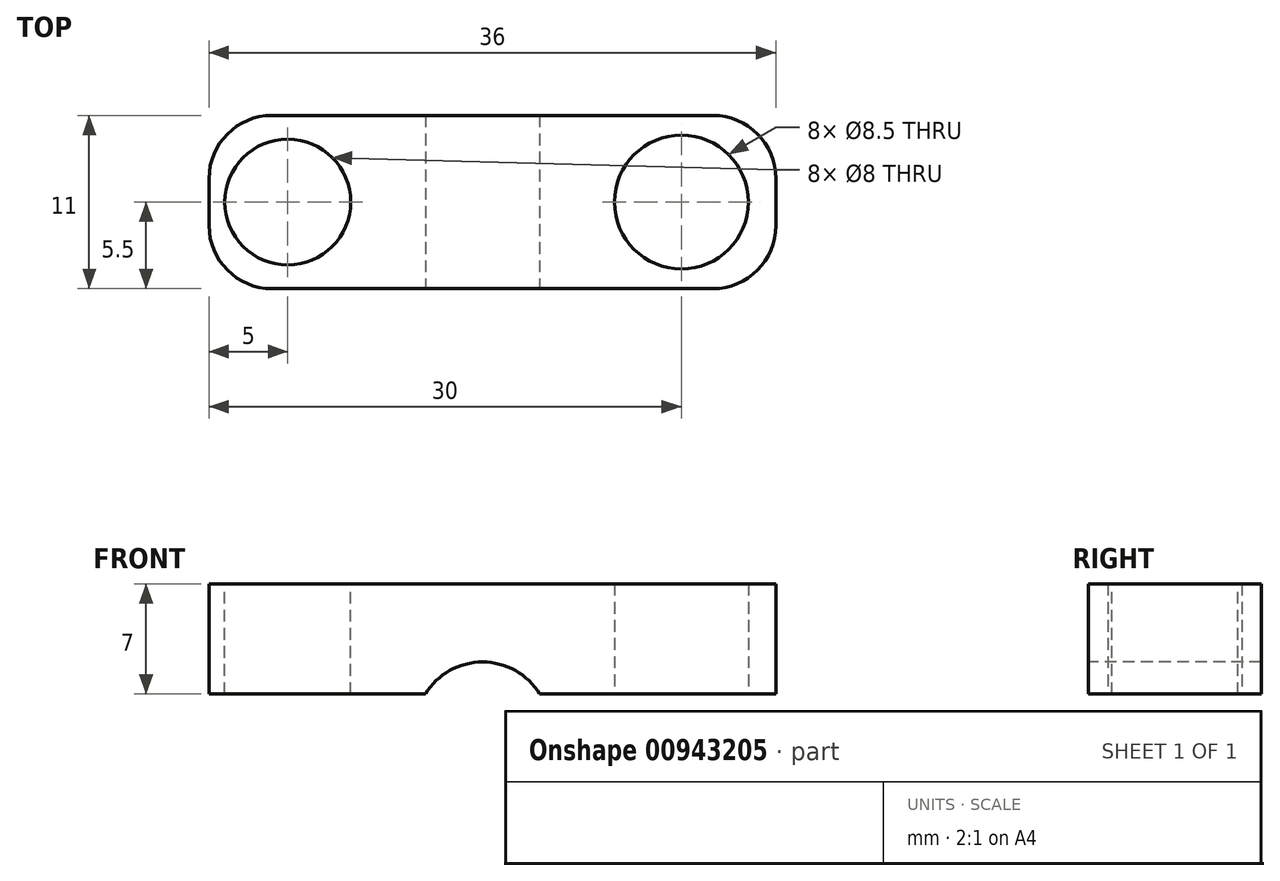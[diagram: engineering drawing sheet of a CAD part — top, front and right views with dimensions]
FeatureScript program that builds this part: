
annotation { "Feature Type Name" : "Feature", "Feature Type Description" : "" }
export const myFeature = defineFeature(function(context is Context, id is Id, definition is map)
    precondition{}
    {
        {
            var Q0;
            Q0=qCreatedBy(makeId("Top.planeOp"),FACE);
            var sketch = newSketch(context, id + "F0", { "sketchPlane" : qUnion([Q0])});
            skLineSegment(sketch, "E0.bottom", {"start": v(-26, 5.5) * mm, "end": v(2, 5.5) * mm});
            skLineSegment(sketch, "E0.top", {"start": v(-26, -5.5) * mm, "end": v(2, -5.5) * mm});
            skLineSegment(sketch, "E0.left", {"start": v(-30, 1.5) * mm, "end": v(-30, -1.5) * mm});
            skLineSegment(sketch, "E0.right", {"start": v(6, 1.5) * mm, "end": v(6, -1.5) * mm});
            skCircle(sketch, "E1", {"center": v(0, 0) * mm, "radius": 4.25 * mm});
            skPoint(sketch, "E2.visualSharp", {"position": v(-30, 5.5) * mm});
            skArc(sketch, "E2.filletArc", {"start": v(-26, 5.5) * mm, "mid": v(-28.83, 4.33) * mm, "end": v(-30, 1.5) * mm});
            skPoint(sketch, "E3.visualSharp", {"position": v(-30, -5.5) * mm});
            skArc(sketch, "E3.filletArc", {"start": v(-30, -1.5) * mm, "mid": v(-28.83, -4.33) * mm, "end": v(-26, -5.5) * mm});
            skPoint(sketch, "E4.visualSharp", {"position": v(6, -5.5) * mm});
            skArc(sketch, "E4.filletArc", {"start": v(2, -5.5) * mm, "mid": v(4.83, -4.33) * mm, "end": v(6, -1.5) * mm});
            skPoint(sketch, "E5.visualSharp", {"position": v(6, 5.5) * mm});
            skArc(sketch, "E5.filletArc", {"start": v(6, 1.5) * mm, "mid": v(4.83, 4.33) * mm, "end": v(2, 5.5) * mm});
            skSolve(sketch);
        }
        {
            var Q0;
            Q0=makeQuery(id+"F0.imprint","IMPRINT",FACE,{"disambiguationData":[TD([[makeQuery(id+"F0.imprint","IMPRINT",EDGE,{"derivedFrom":sQuery(id+"F0.wireOp",EDGE,"E0.bottom")}),-1.0]])]});
            extrude(context, id + "F1", {"entities" : qUnion([Q0]), "depth" : 7 * mm, "offsetDistance" : 25 * mm});
        }
        {
            var Q0;
            Q0=makeQuery(id+"F1.opExtrude","SWEPT_FACE",FACE,{"disambiguationData":[OSD([sQuery(id+"F0.wireOp",EDGE,"E0.top")])]});
            var sketch = newSketch(context, id + "F2", { "sketchPlane" : qUnion([Q0])});
            skArc(sketch, "E6", {"start": v(-9, 0) * mm, "mid": v(-12.63, 2.04) * mm, "end": v(-16.26, 0) * mm});
            skLineSegment(sketch, "E7", {"start": v(-16.26, 0) * mm, "end": v(-9, 0) * mm});
            skSolve(sketch);
        }
        {
            var Q0;
            Q0=qSketchRegion(id+"F2",true);
            extrude(context, id + "F3", {"entities" : qUnion([Q0]), "operationType" : NewBodyOperationType.REMOVE, "oppositeDirection" : true, "depth" : 25 * mm, "offsetDistance" : 25 * mm});
        }
        {
            var Q0;
            Q0=makeQuery(id+"F1.opExtrude","CAP_FACE",FACE,{"disambiguationData":[OSD([sQuery(id+"F0.wireOp",EDGE,"E0.bottom"),sQuery(id+"F0.wireOp",EDGE,"E0.top"),sQuery(id+"F0.wireOp",EDGE,"E0.left"),sQuery(id+"F0.wireOp",EDGE,"E0.right"),sQuery(id+"F0.wireOp",EDGE,"E1"),sQuery(id+"F0.wireOp",EDGE,"E2.filletArc"),sQuery(id+"F0.wireOp",EDGE,"E3.filletArc"),sQuery(id+"F0.wireOp",EDGE,"E4.filletArc"),sQuery(id+"F0.wireOp",EDGE,"E5.filletArc")])],"isStart":false});
            var sketch = newSketch(context, id + "F4", { "sketchPlane" : qUnion([Q0])});
            skPoint(sketch, "E8", {"position": v(-25, 0) * mm});
            skCircle(sketch, "E9", {"center": v(-25, 0) * mm, "radius": 4 * mm});
            skSolve(sketch);
        }
        {
            var Q0;
            Q0=makeQuery(id+"F4.imprint","IMPRINT",FACE,{"disambiguationData":[TD([[makeQuery(id+"F4.imprint","IMPRINT",EDGE,{"derivedFrom":sQuery(id+"F4.wireOp",EDGE,"E9")}),1.0]])]});
            extrude(context, id + "F5", {"entities" : qUnion([Q0]), "operationType" : NewBodyOperationType.REMOVE, "oppositeDirection" : true, "depth" : 25 * mm, "offsetDistance" : 25 * mm});
        }
    });
